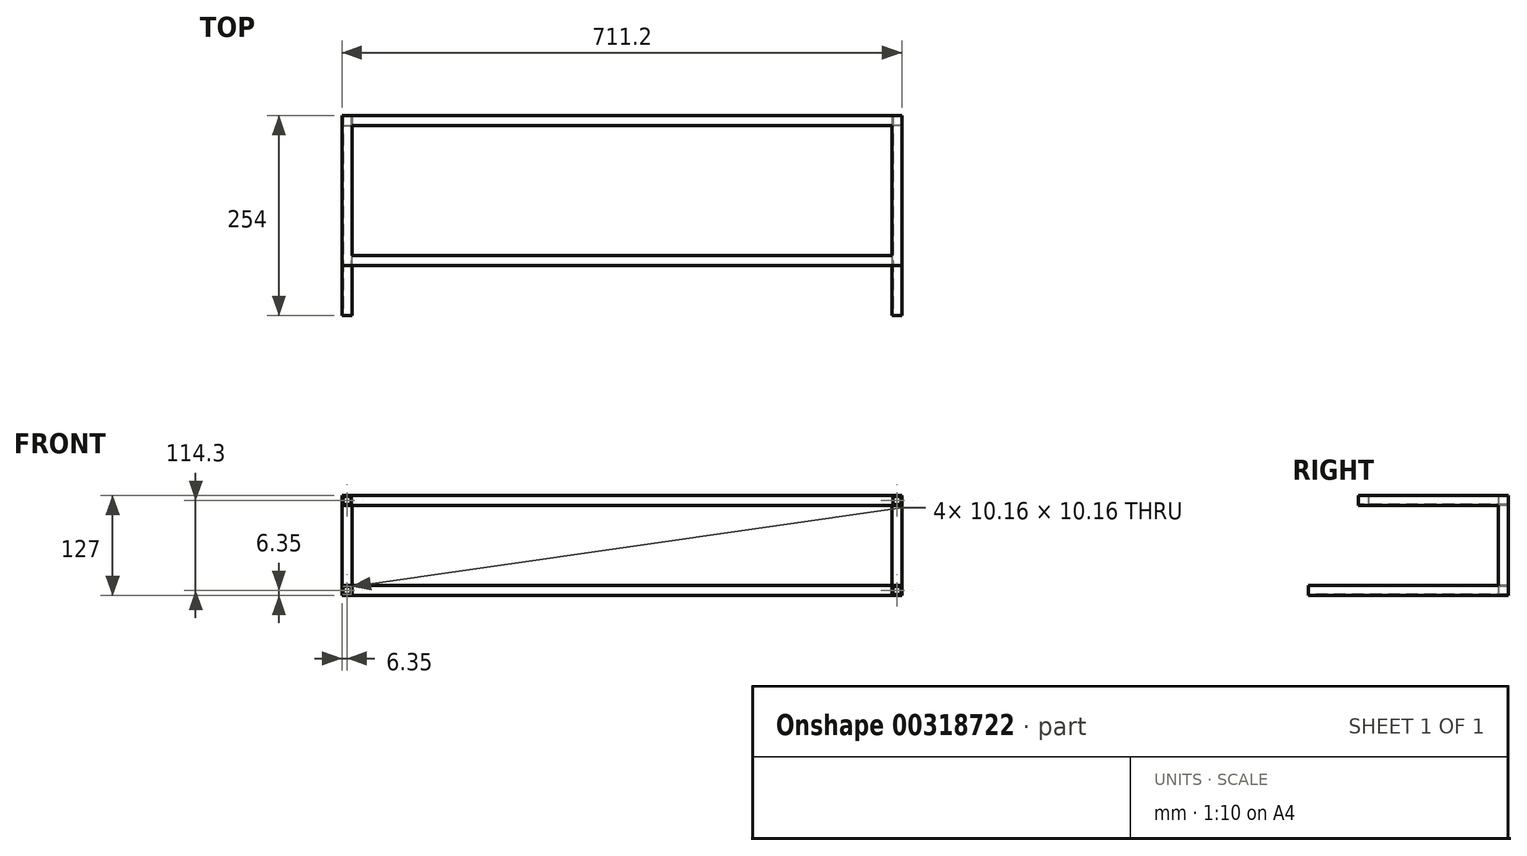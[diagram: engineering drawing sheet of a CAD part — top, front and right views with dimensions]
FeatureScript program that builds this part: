
annotation { "Feature Type Name" : "Feature", "Feature Type Description" : "" }
export const myFeature = defineFeature(function(context is Context, id is Id, definition is map)
    precondition{}
    {
        {
            var Q0;
            Q0=qCreatedBy(makeId("Top.planeOp"),FACE);
            var sketch = newSketch(context, id + "F0", { "sketchPlane" : qUnion([Q0])});
            skLineSegment(sketch, "E0.bottom", {"start": v(0, 0) * mm, "end": v(12.7, 0) * mm});
            skLineSegment(sketch, "E0.top", {"start": v(0, 254) * mm, "end": v(711.2, 254) * mm});
            skLineSegment(sketch, "E0.left", {"start": v(0, 0) * mm, "end": v(0, 254) * mm});
            skLineSegment(sketch, "E0.right", {"start": v(711.2, 0) * mm, "end": v(711.2, 254) * mm});
            skLineSegment(sketch, "E1", {"start": v(12.7, 0) * mm, "end": v(12.7, 241.3) * mm});
            skLineSegment(sketch, "E2", {"start": v(12.7, 241.3) * mm, "end": v(698.5, 241.3) * mm});
            skLineSegment(sketch, "E3", {"start": v(698.5, 241.3) * mm, "end": v(698.5, 0) * mm});
            skLineSegment(sketch, "E4.trimOffspring", {"start": v(698.5, 0) * mm, "end": v(711.2, 0) * mm});
            skSolve(sketch);
        }
        {
            var Q0;
            Q0 = qSketchRegion(id + "F0", true);
            extrude(context, id + "F1", {"entities" : qUnion([Q0]), "depth" : 12.7 * mm});
        }
        {
            var Q0;
            Q0=makeQuery(id+"F1.opExtrude","CAP_FACE",FACE,{"disambiguationData":[OSD([sQuery(id+"F0.wireOp",EDGE,"E0.bottom"),sQuery(id+"F0.wireOp",EDGE,"E0.top"),sQuery(id+"F0.wireOp",EDGE,"E0.left"),sQuery(id+"F0.wireOp",EDGE,"E0.right"),sQuery(id+"F0.wireOp",EDGE,"E1"),sQuery(id+"F0.wireOp",EDGE,"E2"),sQuery(id+"F0.wireOp",EDGE,"E3"),sQuery(id+"F0.wireOp",EDGE,"E4.trimOffspring")])],"isStart":false});
            var sketch = newSketch(context, id + "F2", { "sketchPlane" : qUnion([Q0])});
            skLineSegment(sketch, "E5.bottom", {"start": v(0, 254) * mm, "end": v(12.7, 254) * mm});
            skLineSegment(sketch, "E5.top", {"start": v(0, 241.3) * mm, "end": v(12.7, 241.3) * mm});
            skLineSegment(sketch, "E5.left", {"start": v(0, 254) * mm, "end": v(0, 241.3) * mm});
            skLineSegment(sketch, "E5.right", {"start": v(12.7, 254) * mm, "end": v(12.7, 241.3) * mm});
            skLineSegment(sketch, "E6.bottom", {"start": v(711.2, 254) * mm, "end": v(698.5, 254) * mm});
            skLineSegment(sketch, "E6.top", {"start": v(711.2, 241.3) * mm, "end": v(698.5, 241.3) * mm});
            skLineSegment(sketch, "E6.left", {"start": v(711.2, 254) * mm, "end": v(711.2, 241.3) * mm});
            skLineSegment(sketch, "E6.right", {"start": v(698.5, 254) * mm, "end": v(698.5, 241.3) * mm});
            skSolve(sketch);
        }
        {
            var Q0;
            Q0 = qSketchRegion(id + "F2", true);
            extrude(context, id + "F3", {"entities" : qUnion([Q0]), "operationType" : NewBodyOperationType.ADD, "depth" : 114.3 * mm});
        }
        {
            var Q0;
            Q0=makeQuery(id+"F3.opExtrude","SWEPT_FACE",FACE,{"disambiguationData":[OSD([sQuery(id+"F2.wireOp",EDGE,"E5.top")])]});
            var sketch = newSketch(context, id + "F4", { "sketchPlane" : qUnion([Q0])});
            skLineSegment(sketch, "E7.bottom", {"start": v(0, 127) * mm, "end": v(12.7, 127) * mm});
            skLineSegment(sketch, "E7.top", {"start": v(0, 114.3) * mm, "end": v(12.7, 114.3) * mm});
            skLineSegment(sketch, "E7.left", {"start": v(0, 127) * mm, "end": v(0, 114.3) * mm});
            skLineSegment(sketch, "E7.right", {"start": v(12.7, 127) * mm, "end": v(12.7, 114.3) * mm});
            skSolve(sketch);
        }
        {
            var Q0;
            Q0 = qSketchRegion(id + "F4", true);
            extrude(context, id + "F5", {"entities" : qUnion([Q0]), "operationType" : NewBodyOperationType.ADD, "depth" : 177.8 * mm});
        }
        {
            var Q0;
            Q0=makeQuery(id+"F3.opExtrude","SWEPT_FACE",FACE,{"disambiguationData":[OSD([sQuery(id+"F2.wireOp",EDGE,"E6.top")])]});
            var sketch = newSketch(context, id + "F6", { "sketchPlane" : qUnion([Q0])});
            skLineSegment(sketch, "E8.bottom", {"start": v(698.5, 127) * mm, "end": v(711.2, 127) * mm});
            skLineSegment(sketch, "E8.top", {"start": v(698.5, 114.3) * mm, "end": v(711.2, 114.3) * mm});
            skLineSegment(sketch, "E8.left", {"start": v(698.5, 127) * mm, "end": v(698.5, 114.3) * mm});
            skLineSegment(sketch, "E8.right", {"start": v(711.2, 127) * mm, "end": v(711.2, 114.3) * mm});
            skSolve(sketch);
        }
        {
            var Q0;
            Q0 = qSketchRegion(id + "F6", true);
            extrude(context, id + "F7", {"entities" : qUnion([Q0]), "operationType" : NewBodyOperationType.ADD, "depth" : 177.8 * mm});
        }
        {
            var Q0;
            Q0=makeQuery(id+"F5.boolean.opBoolean","MERGE",FACE,{"derivedFrom":[makeQuery(id+"F3.opExtrude","SWEPT_FACE",FACE,{"disambiguationData":[OSD([sQuery(id+"F2.wireOp",EDGE,"E5.right")])]}),makeQuery(id+"F5.opExtrude","SWEPT_FACE",FACE,{"disambiguationData":[OSD([sQuery(id+"F4.wireOp",EDGE,"E7.right")])]})]});
            var sketch = newSketch(context, id + "F8", { "sketchPlane" : qUnion([Q0])});
            skLineSegment(sketch, "E9.bottom", {"start": v(254, 127) * mm, "end": v(241.3, 127) * mm});
            skLineSegment(sketch, "E9.top", {"start": v(254, 114.3) * mm, "end": v(241.3, 114.3) * mm});
            skLineSegment(sketch, "E9.left", {"start": v(254, 127) * mm, "end": v(254, 114.3) * mm});
            skLineSegment(sketch, "E9.right", {"start": v(241.3, 127) * mm, "end": v(241.3, 114.3) * mm});
            skSolve(sketch);
        }
        {
            var Q0;
            Q0 = qSketchRegion(id + "F8", true);
            extrude(context, id + "F9", {"entities" : qUnion([Q0]), "operationType" : NewBodyOperationType.ADD, "endBound" : BoundingType.UP_TO_NEXT, "depth" : 25.4 * mm});
        }
        {
            var Q0;
            {var subQ1=sQuery(id+"F4.wireOp",EDGE,"E7.right");var subQ2=makeQuery(id+"F5.opExtrude","SWEPT_FACE",FACE,{"disambiguationData":[OSD([subQ1])]});var subQ4=sQuery(id+"F4.wireOp",EDGE,"E7.bottom");var subQ5=sQuery(id+"F2.wireOp",EDGE,"E5.right");var subQ6=makeQuery(id+"F3.opExtrude","SWEPT_FACE",FACE,{"disambiguationData":[OSD([subQ5])]});Q0=makeQuery(id+"F9.boolean.opBoolean","SPLIT",FACE,{"disambiguationData":[TD([makeQuery(id+"F5.opExtrude","SWEPT_FACE",FACE,{"disambiguationData":[OSD([subQ4])]})])],"derivedFrom":makeQuery(id+"F5.boolean.opBoolean","MERGE",FACE,{"derivedFrom":[subQ6,subQ2]})});}
            var sketch = newSketch(context, id + "F10", { "sketchPlane" : qUnion([Q0])});
            skLineSegment(sketch, "E10.bottom", {"start": v(63.5, 127) * mm, "end": v(76.2, 127) * mm});
            skLineSegment(sketch, "E10.top", {"start": v(63.5, 114.3) * mm, "end": v(76.2, 114.3) * mm});
            skLineSegment(sketch, "E10.left", {"start": v(63.5, 127) * mm, "end": v(63.5, 114.3) * mm});
            skLineSegment(sketch, "E10.right", {"start": v(76.2, 127) * mm, "end": v(76.2, 114.3) * mm});
            skSolve(sketch);
        }
        {
            var Q0;
            Q0 = qSketchRegion(id + "F10", true);
            extrude(context, id + "F11", {"entities" : qUnion([Q0]), "operationType" : NewBodyOperationType.ADD, "endBound" : BoundingType.UP_TO_NEXT, "depth" : 25.4 * mm});
        }
        {
            var Q0;
            Q0=makeQuery(id+"F1.opExtrude","SWEPT_FACE",FACE,{"disambiguationData":[OSD([sQuery(id+"F0.wireOp",EDGE,"E4.trimOffspring")])]});
            var sketch = newSketch(context, id + "F12", { "sketchPlane" : qUnion([Q0])});
            skLineSegment(sketch, "E11.bottom", {"start": v(699.77, 11.43) * mm, "end": v(709.93, 11.43) * mm});
            skLineSegment(sketch, "E11.top", {"start": v(699.77, 1.27) * mm, "end": v(709.93, 1.27) * mm});
            skLineSegment(sketch, "E11.left", {"start": v(699.77, 11.43) * mm, "end": v(699.77, 1.27) * mm});
            skLineSegment(sketch, "E11.right", {"start": v(709.93, 11.43) * mm, "end": v(709.93, 1.27) * mm});
            skSolve(sketch);
        }
        {
            var Q0;
            Q0 = qSketchRegion(id + "F12", true);
            extrude(context, id + "F13", {"entities" : qUnion([Q0]), "operationType" : NewBodyOperationType.REMOVE, "endBound" : BoundingType.THROUGH_ALL, "oppositeDirection" : true, "depth" : 25.4 * mm});
        }
        {
            var Q0;
            Q0=makeQuery(id+"F11.boolean.opBoolean","MERGE",FACE,{"derivedFrom":[makeQuery(id+"F5.opExtrude","CAP_FACE",FACE,{"disambiguationData":[OSD([sQuery(id+"F4.wireOp",EDGE,"E7.bottom"),sQuery(id+"F4.wireOp",EDGE,"E7.top"),sQuery(id+"F4.wireOp",EDGE,"E7.left"),sQuery(id+"F4.wireOp",EDGE,"E7.right")])],"isStart":false}),makeQuery(id+"F7.opExtrude","CAP_FACE",FACE,{"disambiguationData":[OSD([sQuery(id+"F6.wireOp",EDGE,"E8.bottom"),sQuery(id+"F6.wireOp",EDGE,"E8.top"),sQuery(id+"F6.wireOp",EDGE,"E8.left"),sQuery(id+"F6.wireOp",EDGE,"E8.right")])],"isStart":false}),makeQuery(id+"F11.opExtrude","SWEPT_FACE",FACE,{"disambiguationData":[OSD([sQuery(id+"F10.wireOp",EDGE,"E10.left")])]})]});
            var sketch = newSketch(context, id + "F14", { "sketchPlane" : qUnion([Q0])});
            skLineSegment(sketch, "E12.bottom", {"start": v(709.93, 125.73) * mm, "end": v(699.77, 125.73) * mm});
            skLineSegment(sketch, "E12.top", {"start": v(709.93, 115.57) * mm, "end": v(699.77, 115.57) * mm});
            skLineSegment(sketch, "E12.left", {"start": v(709.93, 125.73) * mm, "end": v(709.93, 115.57) * mm});
            skLineSegment(sketch, "E12.right", {"start": v(699.77, 125.73) * mm, "end": v(699.77, 115.57) * mm});
            skLineSegment(sketch, "E13.bottom", {"start": v(1.27, 125.73) * mm, "end": v(11.43, 125.73) * mm});
            skLineSegment(sketch, "E13.top", {"start": v(1.27, 115.57) * mm, "end": v(11.43, 115.57) * mm});
            skLineSegment(sketch, "E13.left", {"start": v(1.27, 125.73) * mm, "end": v(1.27, 115.57) * mm});
            skLineSegment(sketch, "E13.right", {"start": v(11.43, 125.73) * mm, "end": v(11.43, 115.57) * mm});
            skSolve(sketch);
        }
        {
            var Q0;
            Q0 = qSketchRegion(id + "F14", true);
            extrude(context, id + "F15", {"entities" : qUnion([Q0]), "operationType" : NewBodyOperationType.REMOVE, "endBound" : BoundingType.THROUGH_ALL, "oppositeDirection" : true, "depth" : 25.4 * mm});
        }
        {
            var Q0;
            Q0=makeQuery(id+"F1.opExtrude","SWEPT_FACE",FACE,{"disambiguationData":[OSD([sQuery(id+"F0.wireOp",EDGE,"E0.bottom")])]});
            var sketch = newSketch(context, id + "F16", { "sketchPlane" : qUnion([Q0])});
            skLineSegment(sketch, "E14.bottom", {"start": v(1.27, 11.43) * mm, "end": v(11.43, 11.43) * mm});
            skLineSegment(sketch, "E14.top", {"start": v(1.27, 1.27) * mm, "end": v(11.43, 1.27) * mm});
            skLineSegment(sketch, "E14.left", {"start": v(1.27, 11.43) * mm, "end": v(1.27, 1.27) * mm});
            skLineSegment(sketch, "E14.right", {"start": v(11.43, 11.43) * mm, "end": v(11.43, 1.27) * mm});
            skSolve(sketch);
        }
        {
            var Q0;
            Q0 = qSketchRegion(id + "F16", true);
            extrude(context, id + "F17", {"entities" : qUnion([Q0]), "operationType" : NewBodyOperationType.REMOVE, "endBound" : BoundingType.THROUGH_ALL, "oppositeDirection" : true, "depth" : 25.4 * mm});
        }
    });
